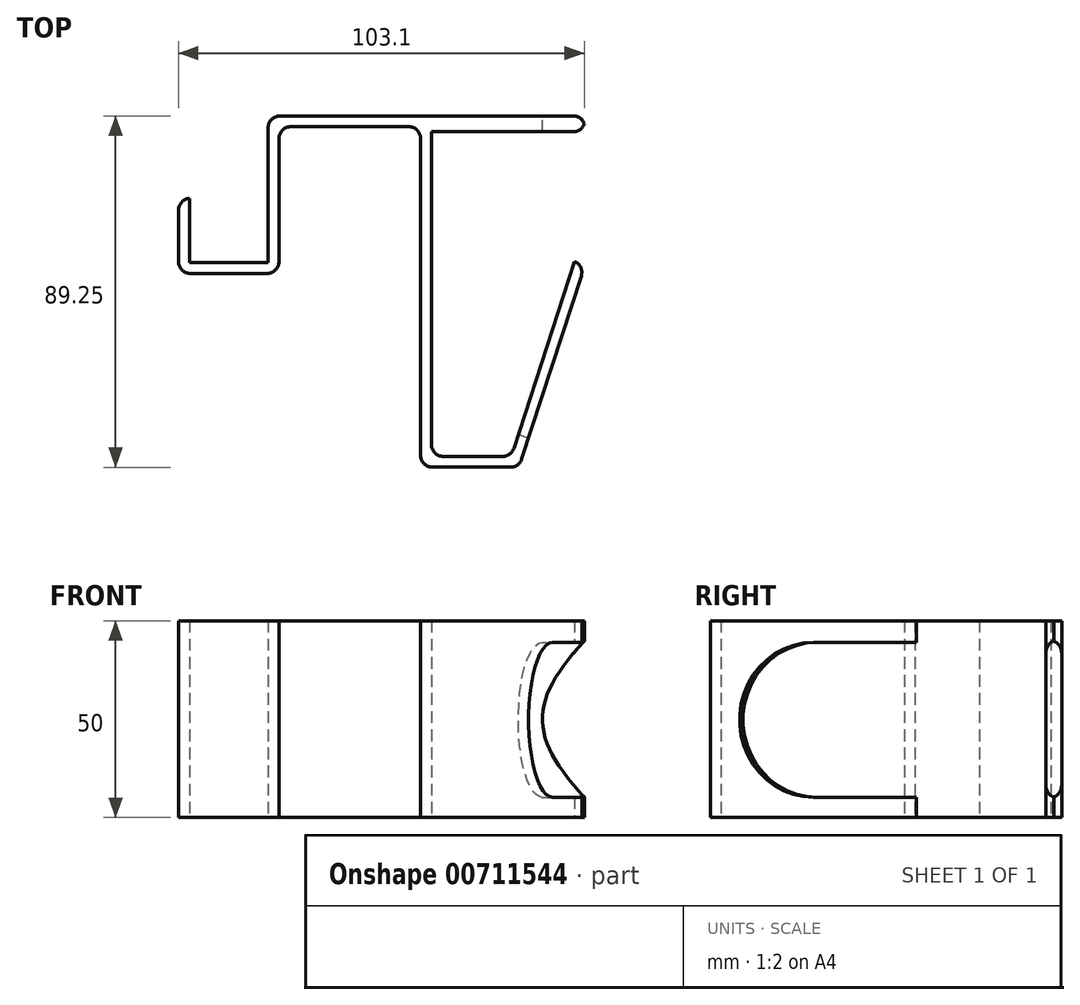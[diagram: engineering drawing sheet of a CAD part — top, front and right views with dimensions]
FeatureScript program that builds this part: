
annotation { "Feature Type Name" : "Feature", "Feature Type Description" : "" }
export const myFeature = defineFeature(function(context is Context, id is Id, definition is map)
    precondition{}
    {
        {
            var Q0;
            Q0=qCreatedBy(makeId("Top.planeOp"),FACE);
            var sketch = newSketch(context, id + "F0", { "sketchPlane" : qUnion([Q0])});
            skLineSegment(sketch, "E0.bottom", {"start": v(-18.93, 51.35) * mm, "end": v(19.82, 51.35) * mm});
            skLineSegment(sketch, "E0.top", {"start": v(-18.93, 11.35) * mm, "end": v(-16.18, 11.35) * mm});
            skLineSegment(sketch, "E0.left", {"start": v(-18.93, 51.35) * mm, "end": v(-18.93, 11.35) * mm});
            skLineSegment(sketch, "E0.right", {"start": v(19.82, 51.35) * mm, "end": v(19.82, 7.7) * mm});
            skLineSegment(sketch, "E1.top", {"start": v(19.82, -37.9) * mm, "end": v(44.82, -37.9) * mm});
            skLineSegment(sketch, "E1.left", {"start": v(19.82, 51.35) * mm, "end": v(19.82, -37.9) * mm});
            skLineSegment(sketch, "E2", {"start": v(-16.18, 11.35) * mm, "end": v(-16.18, 48.6) * mm});
            skLineSegment(sketch, "E3", {"start": v(-16.18, 48.6) * mm, "end": v(19.82, 48.6) * mm});
            skLineSegment(sketch, "E4", {"start": v(19.82, 48.6) * mm, "end": v(19.82, -37.9) * mm});
            skLineSegment(sketch, "E5", {"start": v(44.82, -37.9) * mm, "end": v(61.82, 14.4) * mm});
            skLineSegment(sketch, "E6", {"start": v(19.82, 51.35) * mm, "end": v(22.57, 51.35) * mm});
            skLineSegment(sketch, "E7", {"start": v(22.57, 51.35) * mm, "end": v(22.57, -35.15) * mm});
            skLineSegment(sketch, "E8", {"start": v(22.57, -35.15) * mm, "end": v(42.83, -35.15) * mm});
            skLineSegment(sketch, "E9", {"start": v(42.83, -35.15) * mm, "end": v(58.93, 14.4) * mm});
            skLineSegment(sketch, "E10", {"start": v(58.93, 14.4) * mm, "end": v(61.82, 14.4) * mm});
            skLineSegment(sketch, "E11", {"start": v(-18.93, 11.35) * mm, "end": v(-41.68, 11.35) * mm});
            skLineSegment(sketch, "E12", {"start": v(-41.68, 11.35) * mm, "end": v(-41.68, 30.41) * mm});
            skLineSegment(sketch, "E13", {"start": v(-41.68, 30.41) * mm, "end": v(-38.93, 30.41) * mm});
            skLineSegment(sketch, "E14", {"start": v(-38.93, 30.41) * mm, "end": v(-38.93, 14.1) * mm});
            skLineSegment(sketch, "E15", {"start": v(-38.93, 14.1) * mm, "end": v(-18.93, 14.1) * mm});
            skSolve(sketch);
        }
        {
            var Q0;
            Q0=makeQuery(id+"F0.imprint","IMPRINT",FACE,{"disambiguationData":[TD([[makeQuery(id+"F0.imprint","IMPRINT",EDGE,{"derivedFrom":sQuery(id+"F0.wireOp",EDGE,"E0.bottom")}),-1.0]])]});
            var Q1;
            {var subQ3=sQuery(id+"F0.wireOp",EDGE,"E1.top");Q1=makeQuery(id+"F0.imprint","IMPRINT",FACE,{"disambiguationData":[TD([[makeQuery(id+"F0.imprint","IMPRINT",EDGE,{"derivedFrom":subQ3}),1.0]])]});}
            var Q2;
            {var subQ0=sQuery(id+"F0.wireOp",EDGE,"E11");Q2=makeQuery(id+"F0.imprint","IMPRINT",FACE,{"disambiguationData":[TD([[makeQuery(id+"F0.imprint","IMPRINT",EDGE,{"derivedFrom":subQ0}),-1.0]])]});}
            extrude(context, id + "F1", {"entities" : qUnion([Q0, Q1, Q2]), "depth" : 50 * mm, "offsetDistance" : 25 * mm});
        }
        {
            var Q0;
            Q0=makeQuery(id+"F1.opExtrude","SWEPT_FACE",FACE,{"disambiguationData":[OSD([sQuery(id+"F0.wireOp",EDGE,"E5")])]});
            var sketch = newSketch(context, id + "F2", { "sketchPlane" : qUnion([Q0])});
            skLineSegment(sketch, "E16", {"start": v(32.81, 5.16) * mm, "end": v(5.31, 5.16) * mm});
            skLineSegment(sketch, "E17", {"start": v(32.81, 44.51) * mm, "end": v(5.31, 44.51) * mm});
            skLineSegment(sketch, "E18.0.0", {"start": v(-22.19, 0) * mm, "end": v(32.81, 0) * mm});
            skLineSegment(sketch, "E18.0.1", {"start": v(32.81, 0) * mm, "end": v(32.81, 50) * mm});
            skLineSegment(sketch, "E18.0.2", {"start": v(32.81, 50) * mm, "end": v(-22.19, 50) * mm});
            skLineSegment(sketch, "E18.0.3", {"start": v(-22.19, 50) * mm, "end": v(-22.19, 0) * mm});
            skArc(sketch, "E19", {"start": v(5.31, 44.51) * mm, "mid": v(-14.37, 24.84) * mm, "end": v(5.31, 5.16) * mm});
            skSolve(sketch);
        }
        {
            var Q0;
            {var subQ0=sQuery(id+"F2.wireOp",EDGE,"E16");Q0=makeQuery(id+"F2.imprint","IMPRINT",FACE,{"disambiguationData":[TD([[makeQuery(id+"F2.imprint","IMPRINT",EDGE,{"derivedFrom":subQ0}),-1.0]])]});}
            extrude(context, id + "F3", {"entities" : qUnion([Q0]), "operationType" : NewBodyOperationType.REMOVE, "oppositeDirection" : true, "depth" : 25 * mm, "offsetDistance" : 25 * mm});
        }
        {
            var Q0;
            Q0=makeQuery(id+"F1.opExtrude","SWEPT_FACE",FACE,{"disambiguationData":[OSD([sQuery(id+"F0.wireOp",EDGE,"E0.bottom"),sQuery(id+"F0.wireOp",EDGE,"E6")])]});
            var sketch = newSketch(context, id + "F4", { "sketchPlane" : qUnion([Q0])});
            skLineSegment(sketch, "E20.bottom", {"start": v(-22.57, 50) * mm, "end": v(-61.59, 50) * mm});
            skLineSegment(sketch, "E20.top", {"start": v(-22.57, 0) * mm, "end": v(-61.59, 0) * mm});
            skLineSegment(sketch, "E20.left", {"start": v(-22.57, 50) * mm, "end": v(-22.57, 0) * mm});
            skLineSegment(sketch, "E20.right", {"start": v(-61.59, 50) * mm, "end": v(-61.59, 0) * mm});
            skFitSpline(sketch, "E21", {"points": [v(-61.59, 45) * mm, v(-61.59, 5) * mm], "startDerivative": vector(43.11, -45.55) * mm, "endDerivative": vector(-43.6, -46.54) * mm});
            skPoint(sketch, "E22", {"position": v(18.93, 25) * mm});
            skLineSegment(sketch, "E23", {"start": v(18.93, 25) * mm, "end": v(-108.3, 25) * mm, "construction": true});
            skSolve(sketch);
        }
        {
            var Q0;
            {var subQ1=sQuery(id+"F4.wireOp",EDGE,"E20.bottom");Q0=makeQuery(id+"F4.imprint","IMPRINT",FACE,{"disambiguationData":[TD([[makeQuery(id+"F4.imprint","IMPRINT",EDGE,{"derivedFrom":subQ1}),1.0]])]});}
            extrude(context, id + "F5", {"entities" : qUnion([Q0]), "operationType" : NewBodyOperationType.ADD, "oppositeDirection" : true, "depth" : 4 * mm, "offsetDistance" : 25 * mm});
        }
        {
            var Q0;
            Q0=makeQuery(id+"F1.opExtrude","SWEPT_EDGE",EDGE,{"disambiguationData":[OSD([sQuery(id+"F0.wireOp",EDGE,"E0.bottom"),sQuery(id+"F0.wireOp",EDGE,"E0.left")])]});
            var Q1;
            Q1=makeQuery(id+"F1.opExtrude","SWEPT_EDGE",EDGE,{"disambiguationData":[OSD([sQuery(id+"F0.wireOp",EDGE,"E2"),sQuery(id+"F0.wireOp",EDGE,"E3")])]});
            var Q2;
            Q2=makeQuery(id+"F1.opExtrude","SWEPT_EDGE",EDGE,{"disambiguationData":[OSD([sQuery(id+"F0.wireOp",EDGE,"E1.left"),sQuery(id+"F0.wireOp",EDGE,"E3"),sQuery(id+"F0.wireOp",EDGE,"E4")])]});
            var Q3;
            Q3=makeQuery(id+"F5.opExtrude","CAP_EDGE",EDGE,{"disambiguationData":[OSD([sQuery(id+"F4.wireOp",EDGE,"E20.left")])],"isStart":false});
            var Q4;
            {var subQ0=sQuery(id+"F4.wireOp",EDGE,"E20.right");Q4=makeQuery(id+"F5.opExtrude","CAP_EDGE",EDGE,{"disambiguationData":[OSD([subQ0]),TDD([makeQuery(id+"F4.imprint","IMPRINT",EDGE,{"disambiguationData":[TD([[makeQuery(id+"F4.imprint","INTERSECT",VERTEX,{"derivedFrom":[sQuery(id+"F4.wireOp",EDGE,"E20.top"),subQ0]}),1.0]])],"derivedFrom":subQ0})])],"isStart":true});}
            var Q5;
            {var subQ0=sQuery(id+"F4.wireOp",EDGE,"E20.right");Q5=makeQuery(id+"F5.opExtrude","CAP_EDGE",EDGE,{"disambiguationData":[OSD([subQ0]),TDD([makeQuery(id+"F4.imprint","IMPRINT",EDGE,{"disambiguationData":[TD([[makeQuery(id+"F4.imprint","INTERSECT",VERTEX,{"derivedFrom":[sQuery(id+"F4.wireOp",EDGE,"E20.bottom"),subQ0]}),-1.0]])],"derivedFrom":subQ0})])],"isStart":true});}
            var Q6;
            {var subQ0=sQuery(id+"F4.wireOp",EDGE,"E20.right");Q6=makeQuery(id+"F5.opExtrude","CAP_EDGE",EDGE,{"disambiguationData":[OSD([subQ0]),TDD([makeQuery(id+"F4.imprint","IMPRINT",EDGE,{"disambiguationData":[TD([[makeQuery(id+"F4.imprint","INTERSECT",VERTEX,{"derivedFrom":[sQuery(id+"F4.wireOp",EDGE,"E20.top"),subQ0]}),1.0]])],"derivedFrom":subQ0})])],"isStart":false});}
            var Q7;
            {var subQ0=sQuery(id+"F4.wireOp",EDGE,"E20.right");Q7=makeQuery(id+"F5.opExtrude","CAP_EDGE",EDGE,{"disambiguationData":[OSD([subQ0]),TDD([makeQuery(id+"F4.imprint","IMPRINT",EDGE,{"disambiguationData":[TD([[makeQuery(id+"F4.imprint","INTERSECT",VERTEX,{"derivedFrom":[sQuery(id+"F4.wireOp",EDGE,"E20.bottom"),subQ0]}),-1.0]])],"derivedFrom":subQ0})])],"isStart":false});}
            var Q8;
            Q8=makeQuery(id+"F1.opExtrude","SWEPT_EDGE",EDGE,{"disambiguationData":[OSD([sQuery(id+"F0.wireOp",EDGE,"E0.top"),sQuery(id+"F0.wireOp",EDGE,"E2")])]});
            var Q9;
            Q9=makeQuery(id+"F1.opExtrude","SWEPT_EDGE",EDGE,{"disambiguationData":[OSD([sQuery(id+"F0.wireOp",EDGE,"E11"),sQuery(id+"F0.wireOp",EDGE,"E12")])]});
            var Q10;
            Q10=makeQuery(id+"F1.opExtrude","SWEPT_EDGE",EDGE,{"disambiguationData":[OSD([sQuery(id+"F0.wireOp",EDGE,"E12"),sQuery(id+"F0.wireOp",EDGE,"E13")])]});
            var Q11;
            Q11=makeQuery(id+"F1.opExtrude","SWEPT_EDGE",EDGE,{"disambiguationData":[OSD([sQuery(id+"F0.wireOp",EDGE,"E7"),sQuery(id+"F0.wireOp",EDGE,"E8")])]});
            var Q12;
            Q12=makeQuery(id+"F1.opExtrude","SWEPT_EDGE",EDGE,{"disambiguationData":[OSD([sQuery(id+"F0.wireOp",EDGE,"E8"),sQuery(id+"F0.wireOp",EDGE,"E9")])]});
            var Q13;
            Q13=makeQuery(id+"F1.opExtrude","SWEPT_EDGE",EDGE,{"disambiguationData":[OSD([sQuery(id+"F0.wireOp",EDGE,"E1.top"),sQuery(id+"F0.wireOp",EDGE,"E4")])]});
            var Q14;
            Q14=makeQuery(id+"F1.opExtrude","SWEPT_EDGE",EDGE,{"disambiguationData":[OSD([sQuery(id+"F0.wireOp",EDGE,"E1.top"),sQuery(id+"F0.wireOp",EDGE,"E5")])]});
            var Q15;
            {var subQ0=sQuery(id+"F0.wireOp",EDGE,"E10");var subQ1=sQuery(id+"F0.wireOp",EDGE,"E5");Q15=makeQuery(id+"F3.boolean.opBoolean","SPLIT",EDGE,{"disambiguationData":[TD([makeQuery(id+"F3.opExtrude","SWEPT_FACE",FACE,{"disambiguationData":[OSD([sQuery(id+"F2.wireOp",EDGE,"E16")])]})])],"derivedFrom":makeQuery(id+"F1.opExtrude","SWEPT_EDGE",EDGE,{"disambiguationData":[OSD([subQ1,subQ0])]})});}
            var Q16;
            {var subQ0=sQuery(id+"F0.wireOp",EDGE,"E10");var subQ1=sQuery(id+"F0.wireOp",EDGE,"E5");Q16=makeQuery(id+"F3.boolean.opBoolean","SPLIT",EDGE,{"disambiguationData":[TD([makeQuery(id+"F3.opExtrude","SWEPT_FACE",FACE,{"disambiguationData":[OSD([sQuery(id+"F2.wireOp",EDGE,"E17")])]})])],"derivedFrom":makeQuery(id+"F1.opExtrude","SWEPT_EDGE",EDGE,{"disambiguationData":[OSD([subQ1,subQ0])]})});}
            fillet(context, id + "F6", {"entities" : qUnion([Q0, Q1, Q2, Q3, Q4, Q5, Q6, Q7, Q8, Q9, Q10, Q11, Q12, Q13, Q14, Q15, Q16]), "radius" : 3 * mm, "tangentPropagation" : true, "allowEdgeOverflow" : false});
        }
    });
